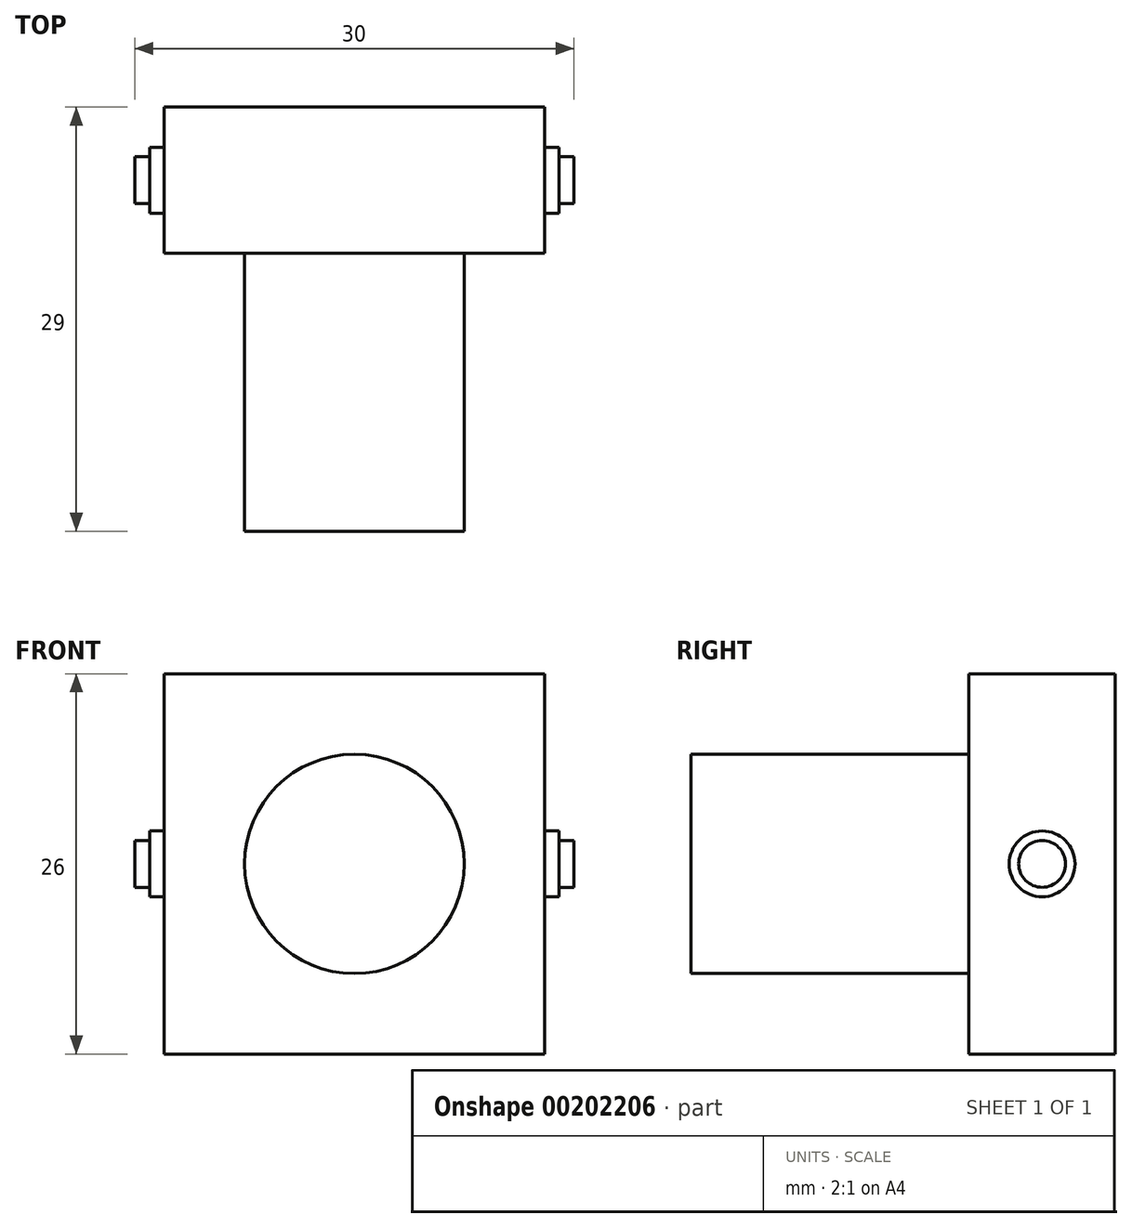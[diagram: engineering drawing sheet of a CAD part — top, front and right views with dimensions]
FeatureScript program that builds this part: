
annotation { "Feature Type Name" : "Feature", "Feature Type Description" : "" }
export const myFeature = defineFeature(function(context is Context, id is Id, definition is map)
    precondition{}
    {
        {
            var Q0;
            Q0=qCreatedBy(makeId("Front.planeOp"),FACE);
            var sketch = newSketch(context, id + "F0", { "sketchPlane" : qUnion([Q0])});
            skLineSegment(sketch, "E0.bottom", {"start": v(-13, 13) * mm, "end": v(13, 13) * mm});
            skLineSegment(sketch, "E0.top", {"start": v(-13, -13) * mm, "end": v(13, -13) * mm});
            skLineSegment(sketch, "E0.left", {"start": v(-13, 13) * mm, "end": v(-13, -13) * mm});
            skLineSegment(sketch, "E0.right", {"start": v(13, 13) * mm, "end": v(13, -13) * mm});
            skPoint(sketch, "E0.middle", {"position": v(0, 0) * mm});
            skSolve(sketch);
        }
        {
            var Q0;
            Q0=makeQuery(id+"F0.imprint","IMPRINT",FACE,{"disambiguationData":[TD([[makeQuery(id+"F0.imprint","IMPRINT",EDGE,{"derivedFrom":sQuery(id+"F0.wireOp",EDGE,"E0.bottom")}),-1.0]])]});
            extrude(context, id + "F1", {"entities" : qUnion([Q0]), "depth" : 10 * mm});
        }
        {
            var Q0;
            Q0=makeQuery(id+"F1.opExtrude","CAP_FACE",FACE,{"disambiguationData":[OSD([sQuery(id+"F0.wireOp",EDGE,"E0.bottom"),sQuery(id+"F0.wireOp",EDGE,"E0.top"),sQuery(id+"F0.wireOp",EDGE,"E0.left"),sQuery(id+"F0.wireOp",EDGE,"E0.right")])],"isStart":false});
            var sketch = newSketch(context, id + "F2", { "sketchPlane" : qUnion([Q0])});
            skCircle(sketch, "E1", {"center": v(0, 0) * mm, "radius": 7.5 * mm});
            skSolve(sketch);
        }
        {
            var Q0;
            Q0=qSketchRegion(id+"F2",true);
            extrude(context, id + "F3", {"entities" : qUnion([Q0]), "operationType" : NewBodyOperationType.ADD, "depth" : 19 * mm});
        }
        {
            var Q0;
            Q0=makeQuery(id+"F1.opExtrude","SWEPT_FACE",FACE,{"disambiguationData":[OSD([sQuery(id+"F0.wireOp",EDGE,"E0.right")])]});
            var sketch = newSketch(context, id + "F4", { "sketchPlane" : qUnion([Q0])});
            skLineSegment(sketch, "E2", {"start": v(-10, 0) * mm, "end": v(0, 0) * mm});
            skPoint(sketch, "E3", {"position": v(-5, 0) * mm});
            skCircle(sketch, "E4", {"center": v(-5, 0) * mm, "radius": 2.25 * mm});
            skSolve(sketch);
        }
        {
            var Q0;
            Q0=qSketchRegion(id+"F4",true);
            extrude(context, id + "F5", {"entities" : qUnion([Q0]), "operationType" : NewBodyOperationType.ADD, "depth" : 1 * mm});
        }
        {
            var Q0;
            Q0=makeQuery(id+"F1.opExtrude","SWEPT_FACE",FACE,{"disambiguationData":[OSD([sQuery(id+"F0.wireOp",EDGE,"E0.left")])]});
            var sketch = newSketch(context, id + "F6", { "sketchPlane" : qUnion([Q0])});
            skLineSegment(sketch, "E5", {"start": v(0, 0) * mm, "end": v(10, 0) * mm});
            skPoint(sketch, "E6", {"position": v(5, 0) * mm});
            skCircle(sketch, "E7", {"center": v(5, 0) * mm, "radius": 2.25 * mm});
            skSolve(sketch);
        }
        {
            var Q0;
            Q0=qSketchRegion(id+"F6",true);
            extrude(context, id + "F7", {"entities" : qUnion([Q0]), "operationType" : NewBodyOperationType.ADD, "depth" : 1 * mm});
        }
        {
            var Q0;
            Q0=makeQuery(id+"F7.opExtrude","CAP_FACE",FACE,{"disambiguationData":[OSD([sQuery(id+"F6.wireOp",EDGE,"E7")])],"isStart":false});
            var sketch = newSketch(context, id + "F8", { "sketchPlane" : qUnion([Q0])});
            skCircle(sketch, "E8", {"center": v(5, 0) * mm, "radius": 1.6 * mm});
            skSolve(sketch);
        }
        {
            var Q0;
            Q0=qSketchRegion(id+"F8",true);
            extrude(context, id + "F9", {"entities" : qUnion([Q0]), "operationType" : NewBodyOperationType.ADD, "depth" : 1 * mm});
        }
        {
            var Q0;
            Q0=makeQuery(id+"F5.opExtrude","CAP_FACE",FACE,{"disambiguationData":[OSD([sQuery(id+"F4.wireOp",EDGE,"E4")])],"isStart":false});
            var sketch = newSketch(context, id + "F10", { "sketchPlane" : qUnion([Q0])});
            skCircle(sketch, "E9", {"center": v(-5, 0) * mm, "radius": 1.6 * mm});
            skSolve(sketch);
        }
        {
            var Q0;
            Q0=makeQuery(id+"F10.imprint","IMPRINT",FACE,{"disambiguationData":[TD([[makeQuery(id+"F10.imprint","IMPRINT",EDGE,{"derivedFrom":sQuery(id+"F10.wireOp",EDGE,"E9")}),1.0]])]});
            extrude(context, id + "F11", {"entities" : qUnion([Q0]), "operationType" : NewBodyOperationType.ADD, "depth" : 1 * mm});
        }
    });
